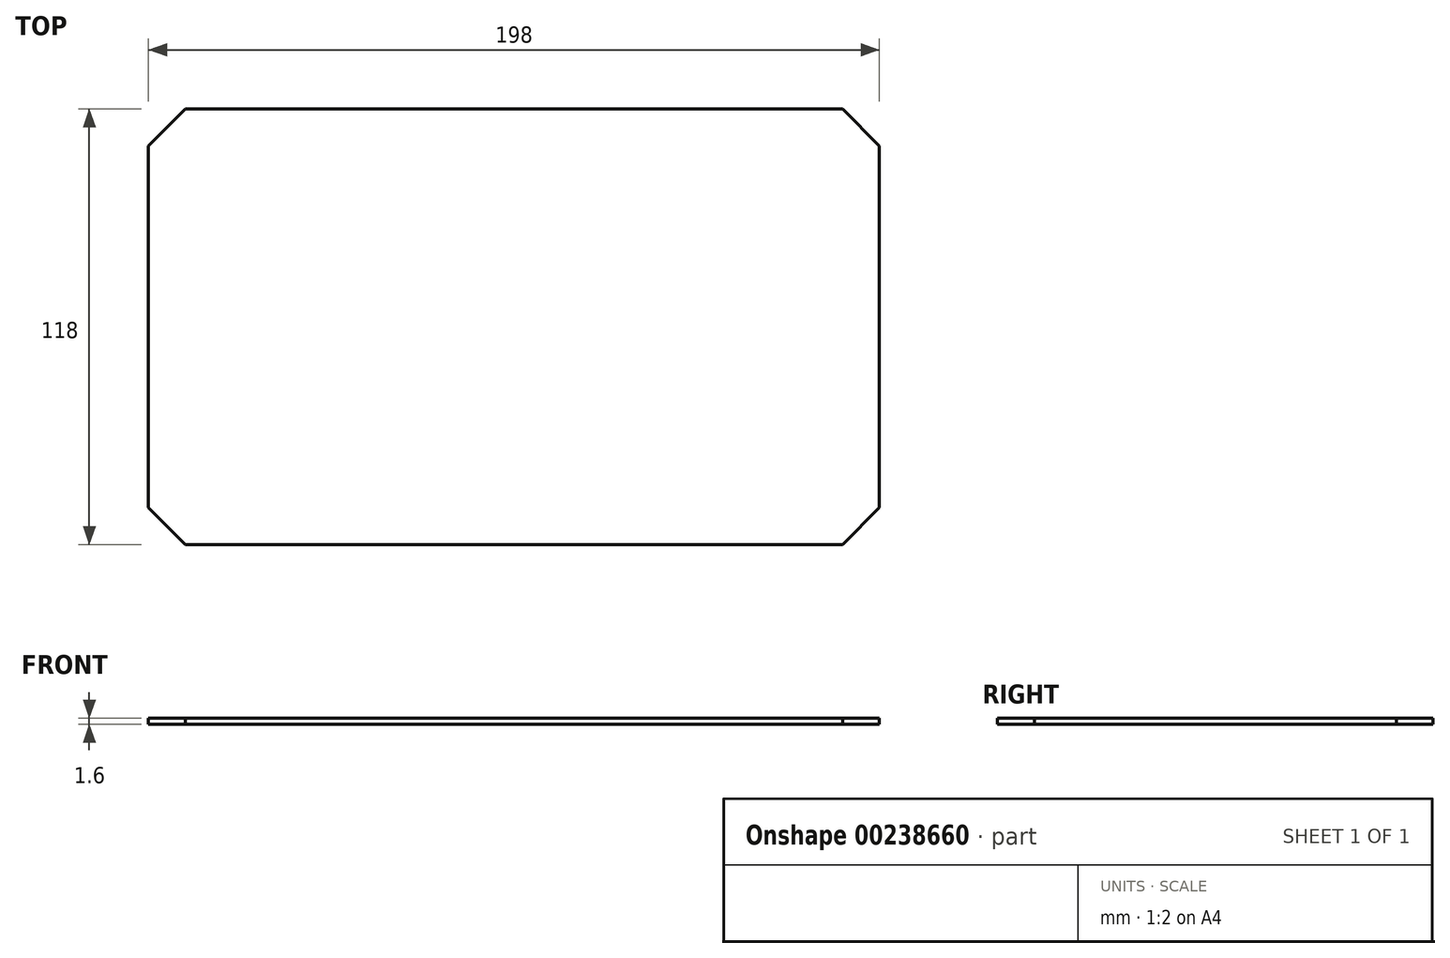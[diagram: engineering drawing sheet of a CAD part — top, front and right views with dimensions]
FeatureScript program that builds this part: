
annotation { "Feature Type Name" : "Feature", "Feature Type Description" : "" }
export const myFeature = defineFeature(function(context is Context, id is Id, definition is map)
    precondition{}
    {
        {
            var Q0;
            Q0=qCreatedBy(makeId("Top.planeOp"),FACE);
            var sketch = newSketch(context, id + "F0", { "sketchPlane" : qUnion([Q0])});
            skLineSegment(sketch, "E0.bottom", {"start": v(89, 59) * mm, "end": v(-89, 59) * mm, "construction": true});
            skLineSegment(sketch, "E0.top", {"start": v(89, -59) * mm, "end": v(-89, -59) * mm, "construction": true});
            skLineSegment(sketch, "E0.left", {"start": v(89, 59) * mm, "end": v(89, -59) * mm, "construction": true});
            skLineSegment(sketch, "E0.right", {"start": v(-89, 59) * mm, "end": v(-89, -59) * mm, "construction": true});
            skPoint(sketch, "E0.middle", {"position": v(0, 0) * mm});
            skLineSegment(sketch, "E1.bottom", {"start": v(-99, 49) * mm, "end": v(99, 49) * mm, "construction": true});
            skLineSegment(sketch, "E1.top", {"start": v(-99, -49) * mm, "end": v(99, -49) * mm, "construction": true});
            skLineSegment(sketch, "E1.left", {"start": v(-99, 49) * mm, "end": v(-99, -49) * mm, "construction": true});
            skLineSegment(sketch, "E1.right", {"start": v(99, 49) * mm, "end": v(99, -49) * mm, "construction": true});
            skLineSegment(sketch, "E2", {"start": v(-99, 49) * mm, "end": v(-89, 59) * mm});
            skLineSegment(sketch, "E3", {"start": v(-89, 59) * mm, "end": v(89, 59) * mm});
            skLineSegment(sketch, "E4", {"start": v(89, 59) * mm, "end": v(99, 49) * mm});
            skLineSegment(sketch, "E5", {"start": v(99, 49) * mm, "end": v(99, -49) * mm});
            skLineSegment(sketch, "E6", {"start": v(99, -49) * mm, "end": v(89, -59) * mm});
            skLineSegment(sketch, "E7", {"start": v(89, -59) * mm, "end": v(-89, -59) * mm});
            skLineSegment(sketch, "E8", {"start": v(-89, -59) * mm, "end": v(-99, -49) * mm});
            skLineSegment(sketch, "E9", {"start": v(-99, -49) * mm, "end": v(-99, 49) * mm});
            skSolve(sketch);
        }
        {
            var Q0;
            Q0 = qSketchRegion(id + "F0", true);
            extrude(context, id + "F1", {"entities" : qUnion([Q0]), "depth" : 1.6 * mm});
        }
    });
